# Revit family: Seating-LAMMHULTS-Archal_XL-Conference-Armchair-Swivel_Base-5_Feet
name_source: partatom
category: Furniture
revit_build: Autodesk Revit 2017 (Build: 20170816_0615(x64)
units: mm (PartAtom-declared; Revit-internal decimal feet)

## family parameters
Always vertical = Yes
Cut with Voids When Loaded = No
OmniClass Number = 23.40.20.00
OmniClass Title = General Furniture and Specialties
Room Calculation Point = No
Shared = No
Work Plane-Based = No

## types (3) — shared parameters
Armrest = Yes
Assembly Code = E2020
Castor Material = Metal - Chrome - Polished
Description = *Please enter mtrl description here for use in mto*
Keynote = 46.B
Manufacturer = LAMMHULTS
Model = ARCHAL_XL
URL = www.lammhults.se
zero-valued in all types: Depth, Height, Thickness, Width

## per-type parameters (varying)
| type | Armrest Material | Frame Material | Seat Material |
| Fabric Grey | Metal - Graphite - Matte | Metal - Graphite - Matte | Fabric - Graphite Grey Woven |
| Fabric White | Metall - Aluminium - Blank | Metall - Aluminium - Blank | Fabric - Canvas - White |
| Leather | Metall - Aluminium - Blank | Metall - Aluminium - Blank | Leather - Rustical - Brown |

## geometry (parser evidence)
native form markers: Blend x9, Sweep x2
no freeform markers — native parametric forms only
